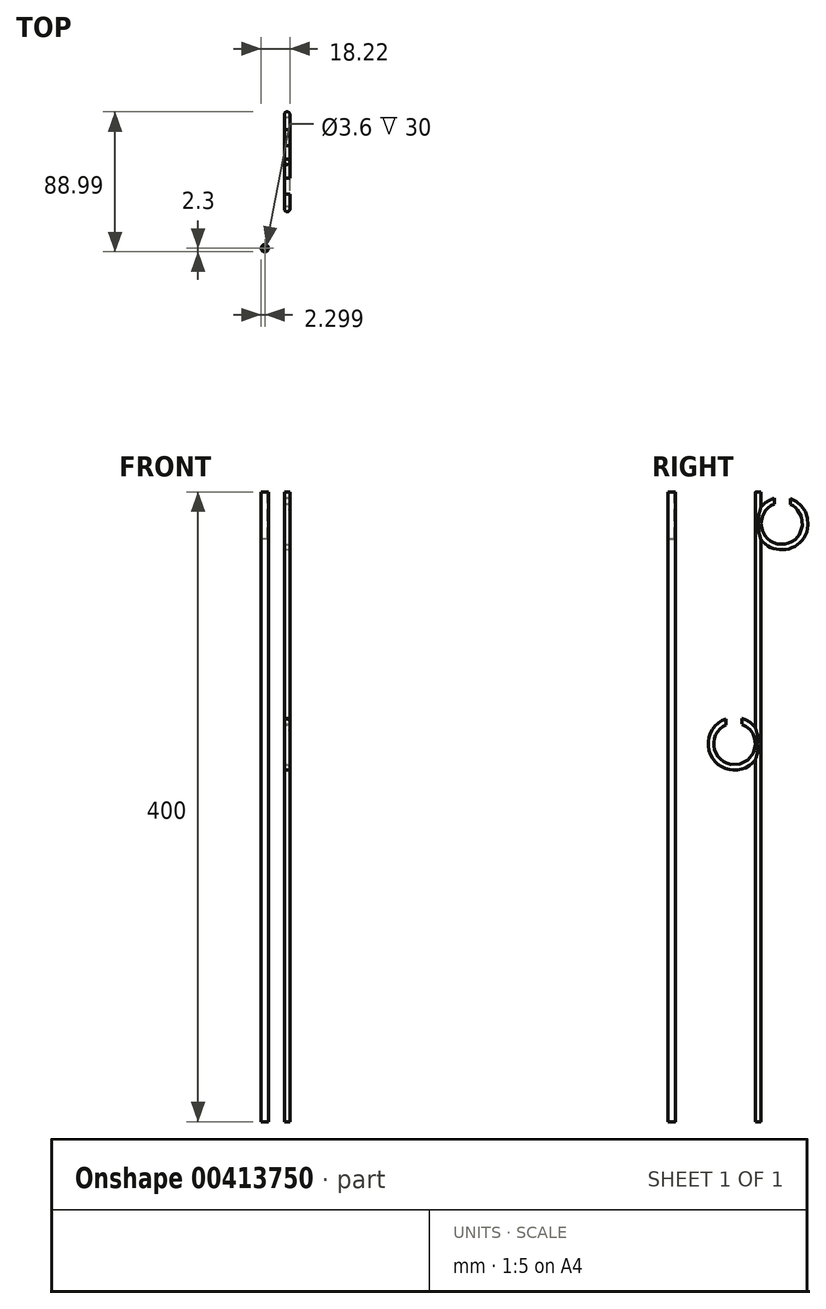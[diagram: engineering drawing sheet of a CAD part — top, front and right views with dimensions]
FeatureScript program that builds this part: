
annotation { "Feature Type Name" : "Feature", "Feature Type Description" : "" }
export const myFeature = defineFeature(function(context is Context, id is Id, definition is map)
    precondition{}
    {
        {
            var Q0;
            Q0=qCreatedBy(makeId("Top.planeOp"),FACE);
            var sketch = newSketch(context, id + "F0", { "sketchPlane" : qUnion([Q0])});
            skCircle(sketch, "E0", {"center": v(0, 0) * mm, "radius": 1.75 * mm});
            skSolve(sketch);
        }
        {
            var Q0;
            Q0=makeQuery(id+"F0.imprint","IMPRINT",FACE,{"disambiguationData":[TD([[makeQuery(id+"F0.imprint","IMPRINT",EDGE,{"derivedFrom":sQuery(id+"F0.wireOp",EDGE,"E0")}),1.0]])]});
            extrude(context, id + "F1", {"entities" : qUnion([Q0]), "endBound" : BoundingType.SYMMETRIC, "depth" : 400 * mm});
        }
        {
            var Q0;
            Q0=qCreatedBy(makeId("Top.planeOp"),FACE);
            cPlane(context, id + "F2", {"entities" : qUnion([Q0]), "cplaneType" : CPlaneType.OFFSET, "offset" : 180 * mm, "width" : 150 * mm, "height" : 150 * mm});
        }
        {
            var Q0;
            Q0=qCreatedBy(id+"F2.planeOp",FACE);
            var sketch = newSketch(context, id + "F3", { "sketchPlane" : qUnion([Q0])});
            skCircle(sketch, "E1", {"center": v(0, 30) * mm, "radius": 1.75 * mm});
            skSolve(sketch);
        }
        {
            var Q0;
            Q0=qCreatedBy(makeId("Right.planeOp"),FACE);
            var sketch = newSketch(context, id + "F4", { "sketchPlane" : qUnion([Q0])});
            skCircle(sketch, "E2", {"center": v(15, 180) * mm, "radius": 15 * mm});
            skLineSegment(sketch, "E3", {"start": v(0, 124.68) * mm, "end": v(0, 178.22) * mm});
            skSolve(sketch);
        }
        {
            var Q0;
            Q0=makeQuery(id+"F3.imprint","IMPRINT",FACE,{"disambiguationData":[TD([[makeQuery(id+"F3.imprint","IMPRINT",EDGE,{"derivedFrom":sQuery(id+"F3.wireOp",EDGE,"E1")}),1.0]])]});
            var Q1;
            Q1=sQuery(id+"F4.wireOp",EDGE,"E2");
            sweep(context, id + "F5", {"operationType" : NewBodyOperationType.ADD, "profiles" : qUnion([Q0]), "path" : qUnion([Q1])});
        }
        {
            var Q0;
            Q0=qCreatedBy(makeId("Top.planeOp"),FACE);
            cPlane(context, id + "F6", {"entities" : qUnion([Q0]), "cplaneType" : CPlaneType.OFFSET, "offset" : 40 * mm, "width" : 150 * mm, "height" : 150 * mm});
        }
        {
            var Q0;
            Q0=qCreatedBy(makeId("Right.planeOp"),FACE);
            var sketch = newSketch(context, id + "F7", { "sketchPlane" : qUnion([Q0])});
            skCircle(sketch, "E4", {"center": v(-15, 40) * mm, "radius": 15 * mm});
            skLineSegment(sketch, "E5", {"start": v(0, 26.45) * mm, "end": v(0, 77.48) * mm});
            skSolve(sketch);
        }
        {
            var Q0;
            Q0=qCreatedBy(id+"F6.planeOp",FACE);
            var sketch = newSketch(context, id + "F8", { "sketchPlane" : qUnion([Q0])});
            skCircle(sketch, "E6", {"center": v(0, -30) * mm, "radius": 1.75 * mm});
            skSolve(sketch);
        }
        {
            var Q0;
            Q0=makeQuery(id+"F8.imprint","IMPRINT",FACE,{"disambiguationData":[TD([[makeQuery(id+"F8.imprint","IMPRINT",EDGE,{"derivedFrom":sQuery(id+"F8.wireOp",EDGE,"E6")}),1.0]])]});
            var Q1;
            Q1=sQuery(id+"F7.wireOp",EDGE,"E4");
            sweep(context, id + "F9", {"operationType" : NewBodyOperationType.ADD, "profiles" : qUnion([Q0]), "path" : qUnion([Q1])});
        }
        {
            var Q0;
            Q0=qCreatedBy(makeId("Right.planeOp"),FACE);
            var sketch = newSketch(context, id + "F10", { "sketchPlane" : qUnion([Q0])});
            skLineSegment(sketch, "E7.bottom", {"start": v(-10.45, 49.73) * mm, "end": v(-20.45, 49.73) * mm});
            skLineSegment(sketch, "E7.top", {"start": v(-10.45, 60.68) * mm, "end": v(-20.45, 60.68) * mm});
            skLineSegment(sketch, "E7.left", {"start": v(-10.45, 49.73) * mm, "end": v(-10.45, 60.68) * mm});
            skLineSegment(sketch, "E7.right", {"start": v(-20.45, 49.73) * mm, "end": v(-20.45, 60.68) * mm});
            skLineSegment(sketch, "E8.bottom", {"start": v(20.32, 190.35) * mm, "end": v(10.32, 190.35) * mm});
            skLineSegment(sketch, "E8.top", {"start": v(20.32, 200.5) * mm, "end": v(10.32, 200.5) * mm});
            skLineSegment(sketch, "E8.left", {"start": v(20.32, 190.35) * mm, "end": v(20.32, 200.5) * mm});
            skLineSegment(sketch, "E8.right", {"start": v(10.32, 190.35) * mm, "end": v(10.32, 200.5) * mm});
            skSolve(sketch);
        }
        {
            var Q0;
            Q0=makeQuery(id+"F10.imprint","IMPRINT",FACE,{"disambiguationData":[TD([[makeQuery(id+"F10.imprint","IMPRINT",EDGE,{"derivedFrom":sQuery(id+"F10.wireOp",EDGE,"E7.bottom")}),-1.0]])]});
            var Q1;
            Q1=makeQuery(id+"F10.imprint","IMPRINT",FACE,{"disambiguationData":[TD([[makeQuery(id+"F10.imprint","IMPRINT",EDGE,{"derivedFrom":sQuery(id+"F10.wireOp",EDGE,"E8.bottom")}),-1.0]])]});
            extrude(context, id + "F11", {"entities" : qUnion([Q0, Q1]), "operationType" : NewBodyOperationType.REMOVE, "endBound" : BoundingType.SYMMETRIC, "oppositeDirection" : true, "depth" : 25 * mm});
        }
        {
            var Q0;
            Q0=qCreatedBy(makeId("Top.planeOp"),FACE);
            var sketch = newSketch(context, id + "F12", { "sketchPlane" : qUnion([Q0])});
            skCircle(sketch, "E9", {"center": v(-14.17, -54.94) * mm, "radius": 2.3 * mm});
            skSolve(sketch);
        }
        {
            var Q0;
            Q0 = qSketchRegion(id + "F12", true);
            extrude(context, id + "F13", {"entities" : qUnion([Q0]), "endBound" : BoundingType.SYMMETRIC, "depth" : 400 * mm});
        }
        {
            var Q0;
            Q0=makeQuery(id+"F13.opExtrude","CAP_FACE",FACE,{"disambiguationData":[OSD([sQuery(id+"F12.wireOp",EDGE,"E9")])],"isStart":false});
            var sketch = newSketch(context, id + "F14", { "sketchPlane" : qUnion([Q0])});
            skCircle(sketch, "E10", {"center": v(-14.17, -54.94) * mm, "radius": 1.8 * mm});
            skSolve(sketch);
        }
        {
            var Q0;
            Q0=makeQuery(id+"F14.imprint","IMPRINT",FACE,{"disambiguationData":[TD([[makeQuery(id+"F14.imprint","IMPRINT",EDGE,{"derivedFrom":sQuery(id+"F14.wireOp",EDGE,"E10")}),1.0]])]});
            extrude(context, id + "F15", {"entities" : qUnion([Q0]), "operationType" : NewBodyOperationType.REMOVE, "oppositeDirection" : true, "depth" : 30 * mm});
        }
    });
